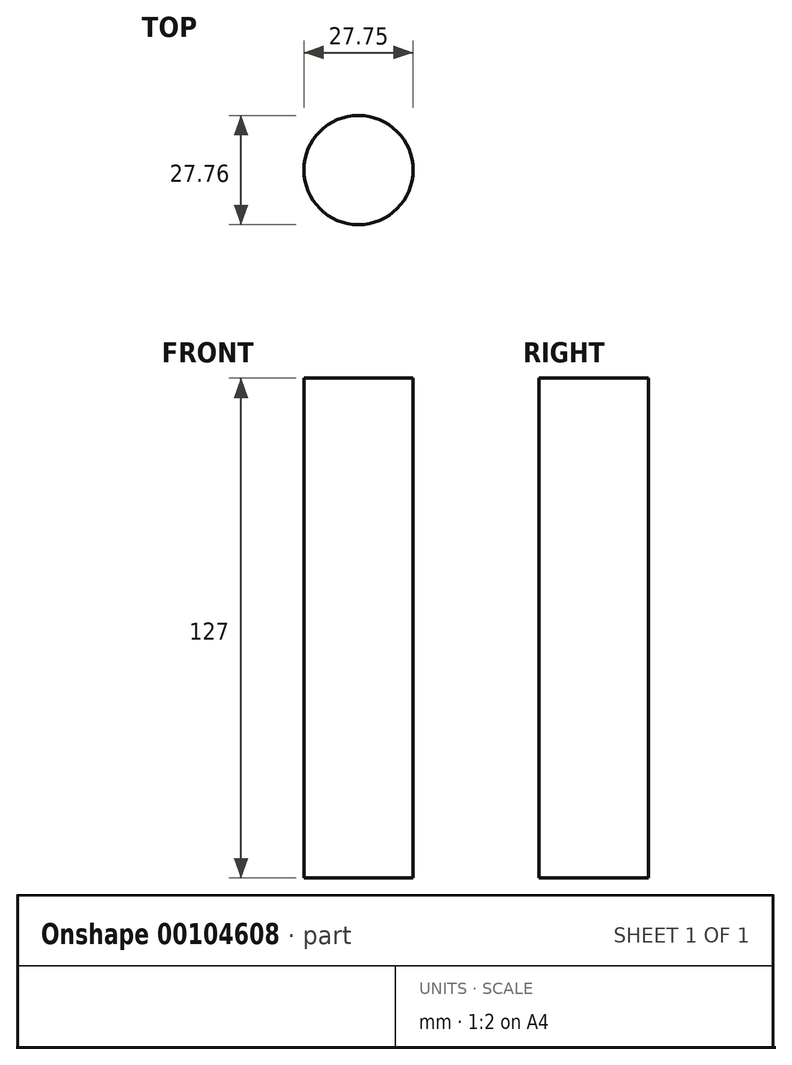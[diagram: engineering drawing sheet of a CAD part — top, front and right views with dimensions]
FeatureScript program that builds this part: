
annotation { "Feature Type Name" : "Feature", "Feature Type Description" : "" }
export const myFeature = defineFeature(function(context is Context, id is Id, definition is map)
    precondition{}
    {
        {
            var Q0;
            Q0=qCreatedBy(makeId("Top.planeOp"),FACE);
            var sketch = newSketch(context, id + "F0", { "sketchPlane" : qUnion([Q0])});
            skCircle(sketch, "E0", {"center": v(3.61, 0) * mm, "radius": 13.88 * mm});
            skSolve(sketch);
        }
        {
            var Q0;
            Q0 = qSketchRegion(id + "F0", true);
            extrude(context, id + "F1", {"entities" : qUnion([Q0]), "depth" : 127 * mm});
        }
    });
